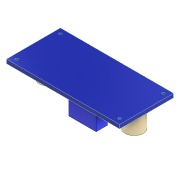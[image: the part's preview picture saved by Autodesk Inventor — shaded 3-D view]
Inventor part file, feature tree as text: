
AUTODESK INVENTOR PART (.ipt)
format: ipt  version: 2022 (Build 260153000, 153)  size: 206,336 bytes
history: native  units: mm
features: extrude x8, sketch x8
ambient origin geometry x8: Origin, YZ Plane, XZ Plane, XY Plane, X Axis, Y Axis, Z Axis, Center Point
bodies: Solid1 (feature_tree), Solid2 (feature_tree), Solid3 (feature_tree), Solid4 (feature_tree), Solid5 (feature_tree), Solid6 (feature_tree), Solid7 (feature_tree)
feature tree (16):
  extrude  "Extrusion1"  Depth=21.0mm
  extrude  "Extrusion2"  Depth=2.0mm
  extrude  "Extrusion3"  Depth=2.0mm
  extrude  "Extrusion4"  Depth=2.0mm
  extrude  "Extrusion5"  Depth=2.0mm
  extrude  "Extrusion6"  Depth=2.0mm
  extrude  "Extrusion7"  Depth=1.02mm
  extrude  "Extrusion8"  Depth=7.774mm TaperAngle=0.0deg
  sketch  "Sketch1"  dims[d0=44.0mm d1=21.0mm]
  sketch  "Sketch2"  dims[d2=2.0mm d3=2.0mm]
  sketch  "Sketch3"  dims[d4=1.02mm d5=2.0mm]
  sketch  "Sketch4"  dims[d6=2.0mm d7=2.0mm]
  sketch  "Sketch5"  dims[d8=2.0mm d9=2.0mm]
  sketch  "Sketch6"  dims[d10=2.0mm d11=1.02mm]
  sketch  "Sketch7"  dims[d12=1.02mm d13=1.02mm]
  sketch  "Sketch8"  dims[d14=1.524mm d15=0.0mm d16=7.774mm d17=0.0mm d18=7.774mm d19=0.0mm d20=7.774mm d21=0.0mm d22=10.0mm d23=10.0mm d24=5.0mm d25=0.0mm d26=7.024mm d27=0.0mm d28=3.0mm d29=0.0mm d30=40.0mm d32=2.0mm d33=20.0mm d35=7.799mm d38=2.0mm d39=0.0mm]
